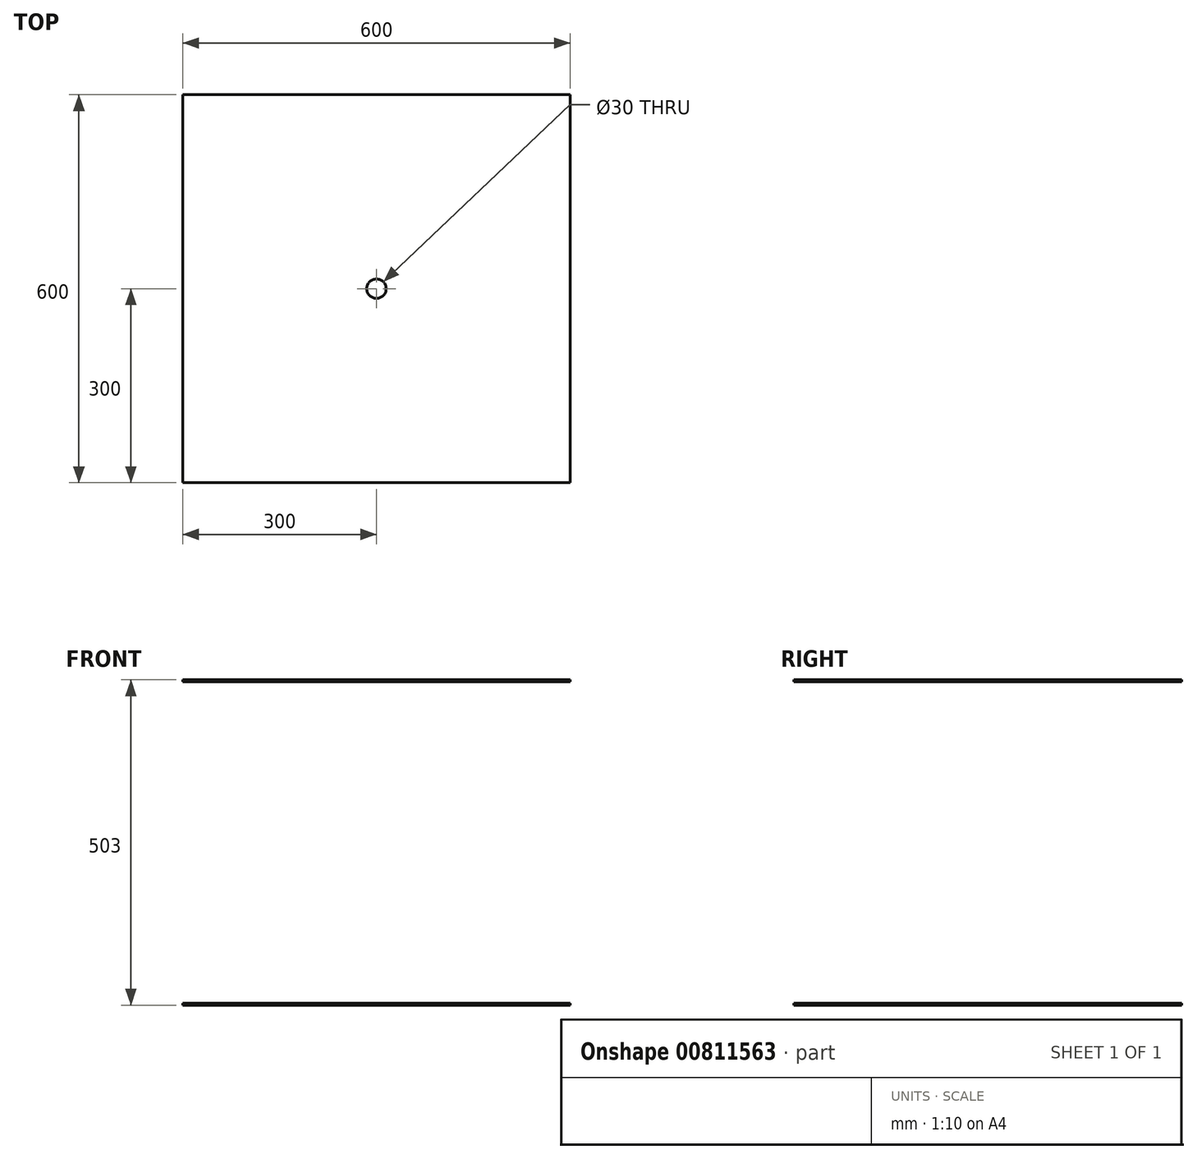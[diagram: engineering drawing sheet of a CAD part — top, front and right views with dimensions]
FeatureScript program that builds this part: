
annotation { "Feature Type Name" : "Feature", "Feature Type Description" : "" }
export const myFeature = defineFeature(function(context is Context, id is Id, definition is map)
    precondition{}
    {
        {
            var Q0;
            Q0=qCreatedBy(makeId("Top.planeOp"),FACE);
            var sketch = newSketch(context, id + "F0", { "sketchPlane" : qUnion([Q0])});
            skLineSegment(sketch, "E0.bottom", {"start": v(300, -300) * mm, "end": v(-300, -300) * mm});
            skLineSegment(sketch, "E0.top", {"start": v(300, 300) * mm, "end": v(-300, 300) * mm});
            skLineSegment(sketch, "E0.left", {"start": v(300, -300) * mm, "end": v(300, 300) * mm});
            skLineSegment(sketch, "E0.right", {"start": v(-300, -300) * mm, "end": v(-300, 300) * mm});
            skPoint(sketch, "E0.middle", {"position": v(0, 0) * mm});
            skSolve(sketch);
        }
        {
            var Q0;
            Q0 = qSketchRegion(id + "F0", true);
            extrude(context, id + "F1", {"entities" : qUnion([Q0]), "depth" : 3 * mm, "offsetDistance" : 25 * mm});
        }
        {
            var Q0;
            Q0=makeQuery(id+"F1.opExtrude","SWEPT_BODY",BODY,{"disambiguationData":[OSD([sQuery(id+"F0.wireOp",EDGE,"E0.bottom"),sQuery(id+"F0.wireOp",EDGE,"E0.top"),sQuery(id+"F0.wireOp",EDGE,"E0.left"),sQuery(id+"F0.wireOp",EDGE,"E0.right")])]});
            transform(context, id + "F2", {"entities" : qUnion([Q0]), "transformType" : TransformType.TRANSLATION_3D, "dx" : 0 * mm, "dy" : 0 * mm, "dz" : 500 * mm, "makeCopy" : true});
        }
        {
            var Q0;
            Q0=makeQuery(id+"F2.opPattern","COPY",FACE,{"derivedFrom":makeQuery(id+"F1.opExtrude","CAP_FACE",FACE,{"disambiguationData":[OSD([sQuery(id+"F0.wireOp",EDGE,"E0.bottom"),sQuery(id+"F0.wireOp",EDGE,"E0.top"),sQuery(id+"F0.wireOp",EDGE,"E0.left"),sQuery(id+"F0.wireOp",EDGE,"E0.right")])],"isStart":false}),"instanceName":"1"});
            var sketch = newSketch(context, id + "F3", { "sketchPlane" : qUnion([Q0])});
            skCircle(sketch, "E1", {"center": v(0, 0) * mm, "radius": 15 * mm});
            skLineSegment(sketch, "E2.bottom", {"start": v(485.63, 275.33) * mm, "end": v(1088.63, 275.33) * mm});
            skLineSegment(sketch, "E2.top", {"start": v(485.63, -327.67) * mm, "end": v(1088.63, -327.67) * mm});
            skLineSegment(sketch, "E2.left", {"start": v(485.63, 275.33) * mm, "end": v(485.63, -327.67) * mm});
            skLineSegment(sketch, "E2.right", {"start": v(1088.63, 275.33) * mm, "end": v(1088.63, -327.67) * mm});
            skCircle(sketch, "E3", {"center": v(775.92, 0) * mm, "radius": 51.93 * mm});
            skSolve(sketch);
        }
        {
            var Q0;
            Q0 = qSketchRegion(id + "F3", true);
            var Q1;
            Q1=makeQuery(id+"F2.opPattern","COPY",FACE,{"derivedFrom":makeQuery(id+"F1.opExtrude","CAP_FACE",FACE,{"disambiguationData":[OSD([sQuery(id+"F0.wireOp",EDGE,"E0.bottom"),sQuery(id+"F0.wireOp",EDGE,"E0.top"),sQuery(id+"F0.wireOp",EDGE,"E0.left"),sQuery(id+"F0.wireOp",EDGE,"E0.right")])],"isStart":true}),"instanceName":"1"});
            extrude(context, id + "F4", {"entities" : qUnion([Q0]), "operationType" : NewBodyOperationType.REMOVE, "endBound" : BoundingType.UP_TO_SURFACE, "oppositeDirection" : true, "depth" : 25 * mm, "endBoundEntityFace" : qUnion([Q1]), "offsetDistance" : 25 * mm});
        }
        {
            var Q0;
            Q0=makeQuery(id+"F1.opExtrude","SWEPT_BODY",BODY,{"disambiguationData":[OSD([sQuery(id+"F0.wireOp",EDGE,"E0.bottom"),sQuery(id+"F0.wireOp",EDGE,"E0.top"),sQuery(id+"F0.wireOp",EDGE,"E0.left"),sQuery(id+"F0.wireOp",EDGE,"E0.right")])]});
            transform(context, id + "F5", {"entities" : qUnion([Q0]), "transformType" : TransformType.TRANSLATION_3D, "dx" : 0 * mm, "dy" : 0 * mm, "dz" : 250 * mm, "makeCopy" : true});
        }
        {
            var Q0;
            Q0=makeQuery(id+"F1.opExtrude","SWEPT_BODY",BODY,{"disambiguationData":[OSD([sQuery(id+"F0.wireOp",EDGE,"E0.bottom"),sQuery(id+"F0.wireOp",EDGE,"E0.top"),sQuery(id+"F0.wireOp",EDGE,"E0.left"),sQuery(id+"F0.wireOp",EDGE,"E0.right")])]});
            transform(context, id + "F6", {"entities" : qUnion([Q0]), "transformType" : TransformType.TRANSLATION_3D, "dx" : 0 * mm, "dy" : 0 * mm, "dz" : -250 * mm, "makeCopy" : true});
        }
        {
            var Q0;
            Q0=makeQuery(id+"F5.opPattern","COPY",BODY,{"derivedFrom":makeQuery(id+"F1.opExtrude","SWEPT_BODY",BODY,{"disambiguationData":[OSD([sQuery(id+"F0.wireOp",EDGE,"E0.bottom"),sQuery(id+"F0.wireOp",EDGE,"E0.top"),sQuery(id+"F0.wireOp",EDGE,"E0.left"),sQuery(id+"F0.wireOp",EDGE,"E0.right")])]}),"instanceName":"1"});
            deleteBodies(context, id + "F7", {"entities" : qUnion([Q0])});
        }
        {
            var Q0;
            Q0=makeQuery(id+"F6.opPattern","COPY",BODY,{"derivedFrom":makeQuery(id+"F1.opExtrude","SWEPT_BODY",BODY,{"disambiguationData":[OSD([sQuery(id+"F0.wireOp",EDGE,"E0.bottom"),sQuery(id+"F0.wireOp",EDGE,"E0.top"),sQuery(id+"F0.wireOp",EDGE,"E0.left"),sQuery(id+"F0.wireOp",EDGE,"E0.right")])]}),"instanceName":"1"});
            transform(context, id + "F8", {"entities" : qUnion([Q0]), "transformType" : TransformType.TRANSLATION_3D, "dx" : 0 * mm, "dy" : 0 * mm, "dz" : -500 * mm, "makeCopy" : true});
        }
        {
            var Q0;
            Q0=makeQuery(id+"F8.opPattern","COPY",FACE,{"derivedFrom":makeQuery(id+"F6.opPattern","COPY",FACE,{"derivedFrom":makeQuery(id+"F1.opExtrude","CAP_FACE",FACE,{"disambiguationData":[OSD([sQuery(id+"F0.wireOp",EDGE,"E0.bottom"),sQuery(id+"F0.wireOp",EDGE,"E0.top"),sQuery(id+"F0.wireOp",EDGE,"E0.left"),sQuery(id+"F0.wireOp",EDGE,"E0.right")])],"isStart":false}),"instanceName":"1"}),"instanceName":"1"});
            var sketch = newSketch(context, id + "F9", { "sketchPlane" : qUnion([Q0])});
            skArc(sketch, "E4", {"start": v(300, -160) * mm, "mid": v(270.26, -190) * mm, "end": v(300, -220) * mm});
            skLineSegment(sketch, "E5", {"start": v(300, -220) * mm, "end": v(300, -160) * mm});
            skSolve(sketch);
        }
        {
            var Q0;
            Q0 = qSketchRegion(id + "F9", true);
            var Q1;
            Q1=makeQuery(id+"F8.opPattern","COPY",FACE,{"derivedFrom":makeQuery(id+"F6.opPattern","COPY",FACE,{"derivedFrom":makeQuery(id+"F1.opExtrude","CAP_FACE",FACE,{"disambiguationData":[OSD([sQuery(id+"F0.wireOp",EDGE,"E0.bottom"),sQuery(id+"F0.wireOp",EDGE,"E0.top"),sQuery(id+"F0.wireOp",EDGE,"E0.left"),sQuery(id+"F0.wireOp",EDGE,"E0.right")])],"isStart":true}),"instanceName":"1"}),"instanceName":"1"});
            extrude(context, id + "F10", {"entities" : qUnion([Q0]), "operationType" : NewBodyOperationType.REMOVE, "endBound" : BoundingType.UP_TO_SURFACE, "oppositeDirection" : true, "depth" : 25 * mm, "endBoundEntityFace" : qUnion([Q1]), "offsetDistance" : 25 * mm});
        }
        {
            var Q0;
            Q0=qCreatedBy(makeId("Top.planeOp"),FACE);
            var sketch = newSketch(context, id + "F11", { "sketchPlane" : qUnion([Q0])});
            skLineSegment(sketch, "E6.bottom", {"start": v(301.5, -301.5) * mm, "end": v(-301.5, -301.5) * mm});
            skLineSegment(sketch, "E6.top", {"start": v(301.5, 301.5) * mm, "end": v(-301.5, 301.5) * mm});
            skLineSegment(sketch, "E6.left", {"start": v(301.5, -301.5) * mm, "end": v(301.5, 301.5) * mm});
            skLineSegment(sketch, "E6.right", {"start": v(-301.5, -301.5) * mm, "end": v(-301.5, 301.5) * mm});
            skPoint(sketch, "E6.middle", {"position": v(0, 0) * mm});
            skSolve(sketch);
        }
        {
            var Q0;
            Q0 = qSketchRegion(id + "F11", true);
            extrude(context, id + "F12", {"entities" : qUnion([Q0]), "depth" : 3 * mm, "offsetDistance" : 25 * mm});
        }
        {
            var Q0;
            Q0=makeQuery(id+"F6.opPattern","COPY",BODY,{"derivedFrom":makeQuery(id+"F1.opExtrude","SWEPT_BODY",BODY,{"disambiguationData":[OSD([sQuery(id+"F0.wireOp",EDGE,"E0.bottom"),sQuery(id+"F0.wireOp",EDGE,"E0.top"),sQuery(id+"F0.wireOp",EDGE,"E0.left"),sQuery(id+"F0.wireOp",EDGE,"E0.right")])]}),"instanceName":"1"});
            deleteBodies(context, id + "F13", {"entities" : qUnion([Q0])});
        }
        {
            var Q0;
            Q0=makeQuery(id+"F8.opPattern","COPY",BODY,{"derivedFrom":makeQuery(id+"F6.opPattern","COPY",BODY,{"derivedFrom":makeQuery(id+"F1.opExtrude","SWEPT_BODY",BODY,{"disambiguationData":[OSD([sQuery(id+"F0.wireOp",EDGE,"E0.bottom"),sQuery(id+"F0.wireOp",EDGE,"E0.top"),sQuery(id+"F0.wireOp",EDGE,"E0.left"),sQuery(id+"F0.wireOp",EDGE,"E0.right")])]}),"instanceName":"1"}),"instanceName":"1"});
            deleteBodies(context, id + "F14", {"entities" : qUnion([Q0])});
        }
        {
            var Q0;
            Q0=makeQuery(id+"F12.opExtrude","SWEPT_BODY",BODY,{"disambiguationData":[OSD([sQuery(id+"F11.wireOp",EDGE,"E6.bottom"),sQuery(id+"F11.wireOp",EDGE,"E6.top"),sQuery(id+"F11.wireOp",EDGE,"E6.left"),sQuery(id+"F11.wireOp",EDGE,"E6.right")])]});
            transform(context, id + "F15", {"entities" : qUnion([Q0]), "transformType" : TransformType.TRANSLATION_3D, "dx" : 0 * mm, "dy" : 0 * mm, "dz" : 0 * mm, "makeCopy" : true});
        }
        {
            var Q0;
            Q0=makeQuery(id+"F12.opExtrude","SWEPT_BODY",BODY,{"disambiguationData":[OSD([sQuery(id+"F11.wireOp",EDGE,"E6.bottom"),sQuery(id+"F11.wireOp",EDGE,"E6.top"),sQuery(id+"F11.wireOp",EDGE,"E6.left"),sQuery(id+"F11.wireOp",EDGE,"E6.right")])]});
            var Q1;
            Q1=makeQuery(id+"F15.opPattern","COPY",BODY,{"derivedFrom":makeQuery(id+"F12.opExtrude","SWEPT_BODY",BODY,{"disambiguationData":[OSD([sQuery(id+"F11.wireOp",EDGE,"E6.bottom"),sQuery(id+"F11.wireOp",EDGE,"E6.top"),sQuery(id+"F11.wireOp",EDGE,"E6.left"),sQuery(id+"F11.wireOp",EDGE,"E6.right")])]}),"instanceName":"1"});
            deleteBodies(context, id + "F16", {"entities" : qUnion([Q0, Q1])});
        }
    });
